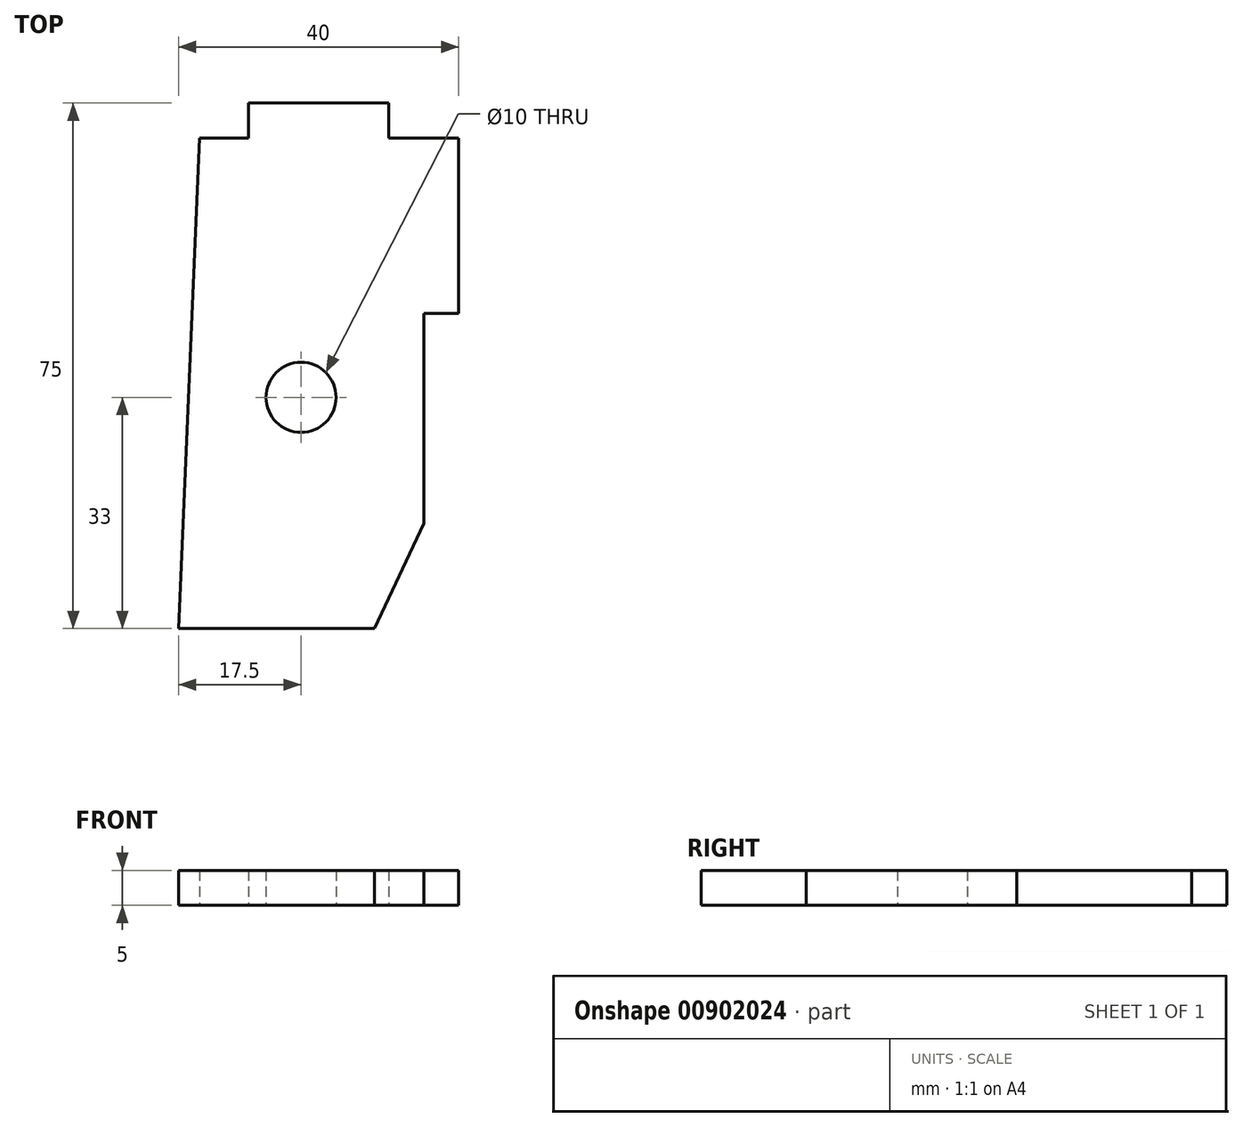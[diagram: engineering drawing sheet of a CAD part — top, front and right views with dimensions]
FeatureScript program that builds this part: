
annotation { "Feature Type Name" : "Feature", "Feature Type Description" : "" }
export const myFeature = defineFeature(function(context is Context, id is Id, definition is map)
    precondition{}
    {
        {
            var Q0;
            Q0=qCreatedBy(makeId("Top.planeOp"),FACE);
            var sketch = newSketch(context, id + "F0", { "sketchPlane" : qUnion([Q0])});
            skLineSegment(sketch, "E0.bottom", {"start": v(-14.5, 70) * mm, "end": v(-7.5, 70) * mm});
            skLineSegment(sketch, "E0.top", {"start": v(-17.5, 0) * mm, "end": v(22.5, 0) * mm});
            skLineSegment(sketch, "E0.right", {"start": v(22.5, 70) * mm, "end": v(22.5, 45) * mm});
            skLineSegment(sketch, "E1.bottom", {"start": v(-7.5, 75) * mm, "end": v(12.5, 75) * mm});
            skLineSegment(sketch, "E1.left", {"start": v(-7.5, 75) * mm, "end": v(-7.5, 70) * mm});
            skLineSegment(sketch, "E1.right", {"start": v(12.5, 75) * mm, "end": v(12.5, 70) * mm});
            skLineSegment(sketch, "E2.trimOffspring", {"start": v(12.5, 70) * mm, "end": v(22.5, 70) * mm});
            skCircle(sketch, "E3", {"center": v(0, 33) * mm, "radius": 5 * mm});
            skLineSegment(sketch, "E4.bottom", {"start": v(22.5, 15) * mm, "end": v(17.5, 15) * mm});
            skLineSegment(sketch, "E4.top", {"start": v(22.5, 45) * mm, "end": v(17.5, 45) * mm});
            skLineSegment(sketch, "E4.right", {"start": v(17.5, 15) * mm, "end": v(17.5, 45) * mm});
            skLineSegment(sketch, "E5.trimOffspring", {"start": v(22.5, 15) * mm, "end": v(22.5, 0) * mm});
            skLineSegment(sketch, "E6", {"start": v(-17.5, 0) * mm, "end": v(-14.5, 70) * mm});
            skSolve(sketch);
        }
        {
            var Q0;
            Q0=makeQuery(id+"F0.imprint","IMPRINT",FACE,{"disambiguationData":[TD([[makeQuery(id+"F0.imprint","IMPRINT",EDGE,{"derivedFrom":sQuery(id+"F0.wireOp",EDGE,"E0.bottom")}),-1.0]])]});
            extrude(context, id + "F1", {"entities" : qUnion([Q0]), "depth" : 5 * mm, "offsetDistance" : 25 * mm});
        }
        {
            var Q0;
            Q0=makeQuery(id+"F1.opExtrude","CAP_FACE",FACE,{"disambiguationData":[OSD([sQuery(id+"F0.wireOp",EDGE,"E0.bottom"),sQuery(id+"F0.wireOp",EDGE,"E0.top"),sQuery(id+"F0.wireOp",EDGE,"E0.right"),sQuery(id+"F0.wireOp",EDGE,"E1.bottom"),sQuery(id+"F0.wireOp",EDGE,"E1.left"),sQuery(id+"F0.wireOp",EDGE,"E1.right"),sQuery(id+"F0.wireOp",EDGE,"E2.trimOffspring"),sQuery(id+"F0.wireOp",EDGE,"E3"),sQuery(id+"F0.wireOp",EDGE,"E4.bottom"),sQuery(id+"F0.wireOp",EDGE,"E4.top"),sQuery(id+"F0.wireOp",EDGE,"E4.right"),sQuery(id+"F0.wireOp",EDGE,"E5.trimOffspring"),sQuery(id+"F0.wireOp",EDGE,"E6")])],"isStart":false});
            var sketch = newSketch(context, id + "F2", { "sketchPlane" : qUnion([Q0])});
            skLineSegment(sketch, "E7", {"start": v(10.5, 0) * mm, "end": v(17.5, 15) * mm});
            skLineSegment(sketch, "E8", {"start": v(17.5, 15) * mm, "end": v(22.5, 15) * mm});
            skLineSegment(sketch, "E9", {"start": v(22.5, 15) * mm, "end": v(22.5, 0) * mm});
            skLineSegment(sketch, "E10", {"start": v(22.5, 0) * mm, "end": v(10.5, 0) * mm});
            skSolve(sketch);
        }
        {
            var Q0;
            Q0 = qSketchRegion(id + "F2", true);
            extrude(context, id + "F3", {"entities" : qUnion([Q0]), "operationType" : NewBodyOperationType.REMOVE, "oppositeDirection" : true, "depth" : 25 * mm, "offsetDistance" : 25 * mm});
        }
    });
